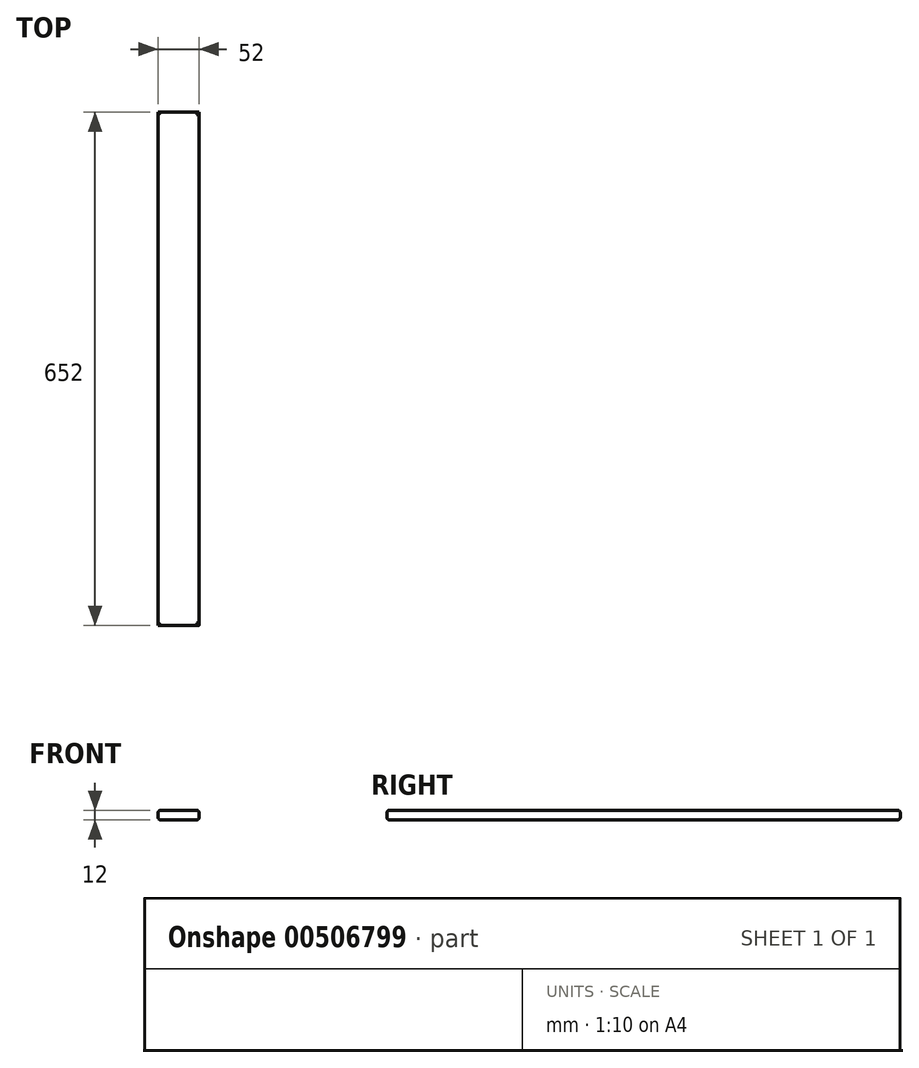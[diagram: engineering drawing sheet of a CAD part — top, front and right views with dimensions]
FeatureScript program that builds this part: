
annotation { "Feature Type Name" : "Feature", "Feature Type Description" : "" }
export const myFeature = defineFeature(function(context is Context, id is Id, definition is map)
    precondition{}
    {
        {
            var Q0;
            Q0=qCreatedBy(makeId("Front.planeOp"),FACE);
            var sketch = newSketch(context, id + "F0", { "sketchPlane" : qUnion([Q0])});
            skLineSegment(sketch, "E0.bottom", {"start": v(-127.13, 29.2) * mm, "end": v(-75.13, 29.2) * mm});
            skLineSegment(sketch, "E0.top", {"start": v(-127.13, 17.2) * mm, "end": v(-75.13, 17.2) * mm});
            skLineSegment(sketch, "E0.left", {"start": v(-127.13, 29.2) * mm, "end": v(-127.13, 17.2) * mm});
            skLineSegment(sketch, "E0.right", {"start": v(-75.13, 29.2) * mm, "end": v(-75.13, 17.2) * mm});
            skSolve(sketch);
        }
        {
            var Q0;
            Q0=makeQuery(id+"F0.imprint","IMPRINT",FACE,{"disambiguationData":[TD([[makeQuery(id+"F0.imprint","IMPRINT",EDGE,{"derivedFrom":sQuery(id+"F0.wireOp",EDGE,"E0.bottom")}),-1.0]])]});
            extrude(context, id + "F1", {"entities" : qUnion([Q0]), "depth" : 652 * mm});
        }
        {
            var Q0;
            Q0=makeQuery(id+"F1.opExtrude","SWEPT_FACE",FACE,{"disambiguationData":[OSD([sQuery(id+"F0.wireOp",EDGE,"E0.bottom")])]});
            var Q1;
            Q1=makeQuery(id+"F1.opExtrude","SWEPT_FACE",FACE,{"disambiguationData":[OSD([sQuery(id+"F0.wireOp",EDGE,"E0.top")])]});
            fillet(context, id + "F2", {"entities" : qUnion([Q0, Q1]), "radius" : 3 * mm, "tangentPropagation" : true, "allowEdgeOverflow" : false});
        }
        {
            var Q0;
            Q0=makeQuery(id+"F1.opExtrude","SWEPT_FACE",FACE,{"disambiguationData":[OSD([sQuery(id+"F0.wireOp",EDGE,"E0.bottom")])]});
            var sketch = newSketch(context, id + "F3", { "sketchPlane" : qUnion([Q0])});
            skLineSegment(sketch, "E1", {"start": v(-124.13, -3) * mm, "end": v(-95.13, -3) * mm});
            skLineSegment(sketch, "E2", {"start": v(-95.13, -3) * mm, "end": v(-95.13, -300) * mm});
            skLineSegment(sketch, "E3", {"start": v(-95.13, -326) * mm, "end": v(-95.13, -649) * mm});
            skLineSegment(sketch, "E4", {"start": v(-95.13, -300) * mm, "end": v(-95.13, -326) * mm});
            skLineSegment(sketch, "E5", {"start": v(-95.13, -3) * mm, "end": v(-78.13, -3) * mm});
            skSolve(sketch);
        }
    });
